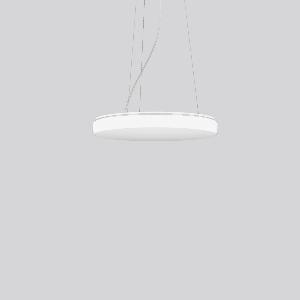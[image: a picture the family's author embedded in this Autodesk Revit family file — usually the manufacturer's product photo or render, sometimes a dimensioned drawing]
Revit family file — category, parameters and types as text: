
# Revit family: flat_polymero_kreis_slim_312091_002_1_76_82e5
name_source: partatom
category: Lighting Fixtures
units: mm (PartAtom-declared; Revit-internal decimal feet)

## family parameters
Cut with Voids When Loaded = No
Host = Face
Light Source = No
Part Type = Normal
Room Calculation Point = No
Round Connector Dimension = Use Diameter
Shared = No

## types (1)
- FLAT POLYMERO KREIS SLIM (1 x LED Modul 830, 3700 lm, 3000)
    Apparent Load = 40 VA
    CIE Flux Codes = 42 72 91 83 100
    Color Rendering = 80
    Color Temperature = 3000
    Default Elevation = 1800 mm
    Description = Series: FLAT POLYMERO KREIS SLIM
Decorative round LED pendant luminaire. Base and canopy: metal, powder-coated, white. Canopy Ø 205 mm, h 35 mm. Diffuser made of non-yellowing plastic (PMMA), opal. Diffuser fastening: patented push system. Homogeneous and smooth light distribution. Suitable for pendant. 3-point steel cable suspension, steplessly adjustable. Special lengths available on request. TouchDim sensor capable. Light and/or presence sensors can be integrated. 
Colour: white
Diameter: 515 mm
Height: 69 mm
Suspension length: 350-1300 mm
Lamp: LED
Socket: without socket
Colour temperature: 3000K
Colour rendering index (CRI): 83
System power: 40 W
Rated luminous flux: 3700 lm
Luminous efficiency: 93 lm/W
Control gear: AC power, DALI dimmable
Protection class: I
Type of protection: IP 40
    Height = 69 mm
    Lamp = 1 x LED Modul 830
    Lamp Light Flux = 3700 lm
    Lamp count = 1
    Length = 515 mm
    Lifetime = 50000 h
    Luminous efficacy = 93 lm/W
    Manufacturer = RZB
    ModVariant = No
    Model = 312091.002.1.76
    Mounting Place = Ceiling
    Mounting Type = Pendant
    Number of Poles = 1
    OnlyDefault = Yes
    Power Factor = 1
    Product Name = FLAT POLYMERO KREIS SLIM
    Product group = Pendant luminaires
    ProductGroupID = 902
    Protection Class = Protection class I
    Protection Degree = IP 40
    RLX_Detail_Level = 1
    RLX_Emergency_Light_Flux = 0 lm
    RLX_Emergency_Type = 0
    RLX_Emergency_Type_DB = No
    RlxData = <blob elided: 42357 chars, md5=2e3e3987>
    Socket = socket
    Standby Power = 0 W
    System Light Flux = 3700 lm
    System Power = 40 W
    Type Comments = Product without accessories
    Type Image = 312091.002.jpg
    URL = http://relux.com
    VarID = ---
    Voltage = 230 V
    Voltage Range = 220-240 V
    Weight = 0.00 kg
    Width = 0 mm  [stored 0 ft]

note: [stored X ft] marks values corroborated as IEEE doubles in the binary element streams (Revit-internal decimal feet)

## geometry (parser evidence)
native form markers: Blend x4, Sweep x10
no freeform markers — native parametric forms only
